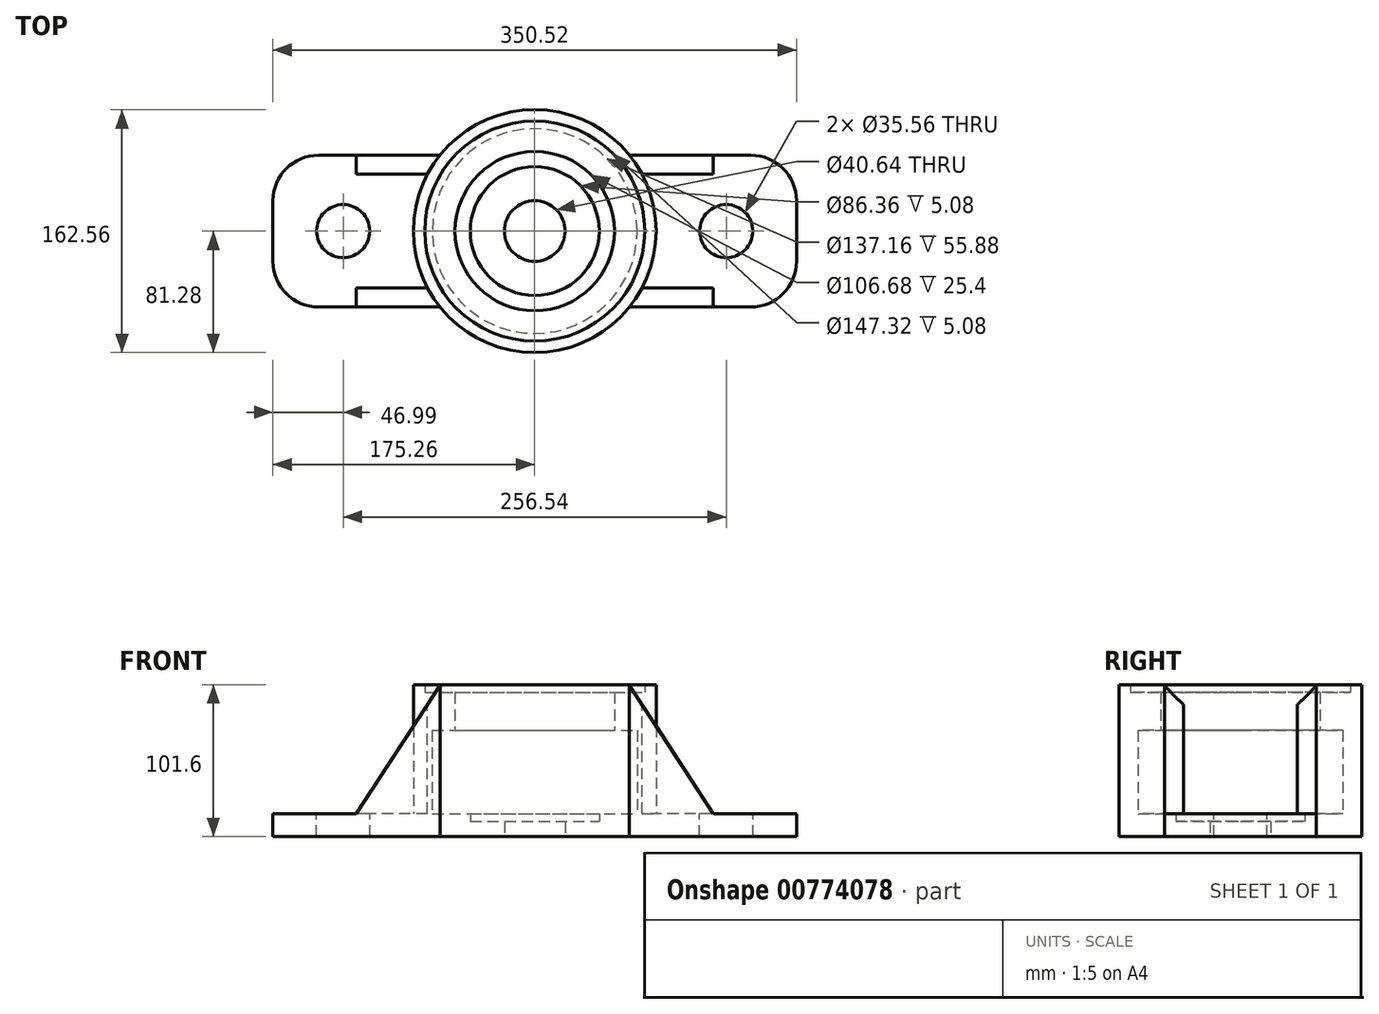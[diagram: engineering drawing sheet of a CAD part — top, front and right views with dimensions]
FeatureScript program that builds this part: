
annotation { "Feature Type Name" : "Feature", "Feature Type Description" : "" }
export const myFeature = defineFeature(function(context is Context, id is Id, definition is map)
    precondition{}
    {
        {
            var Q0;
            Q0=qCreatedBy(makeId("Top.planeOp"),FACE);
            var sketch = newSketch(context, id + "F0", { "sketchPlane" : qUnion([Q0])});
            skLineSegment(sketch, "E0.bottom", {"start": v(175.26, 50.8) * mm, "end": v(-175.26, 50.8) * mm});
            skLineSegment(sketch, "E0.top", {"start": v(175.26, -50.8) * mm, "end": v(-175.26, -50.8) * mm});
            skLineSegment(sketch, "E0.left", {"start": v(175.26, 50.8) * mm, "end": v(175.26, -50.8) * mm});
            skLineSegment(sketch, "E0.right", {"start": v(-175.26, 50.8) * mm, "end": v(-175.26, -50.8) * mm});
            skPoint(sketch, "E0.middle", {"position": v(0, 0) * mm});
            skSolve(sketch);
        }
        {
            var Q0;
            Q0 = qSketchRegion(id + "F0", true);
            extrude(context, id + "F1", {"entities" : qUnion([Q0]), "depth" : 101.6 * mm, "offsetDistance" : 25.4 * mm});
        }
        {
            var Q0;
            Q0=makeQuery(id+"F1.opExtrude","SWEPT_FACE",FACE,{"disambiguationData":[OSD([sQuery(id+"F0.wireOp",EDGE,"E0.top")])]});
            var sketch = newSketch(context, id + "F2", { "sketchPlane" : qUnion([Q0])});
            skLineSegment(sketch, "E1", {"start": v(-175.26, 15.24) * mm, "end": v(-119.38, 15.24) * mm});
            skLineSegment(sketch, "E2", {"start": v(-119.38, 15.24) * mm, "end": v(-63.3, 101.6) * mm});
            skLineSegment(sketch, "E3", {"start": v(63.3, 101.6) * mm, "end": v(119.38, 15.24) * mm});
            skLineSegment(sketch, "E4", {"start": v(119.38, 15.24) * mm, "end": v(175.26, 15.24) * mm});
            skSolve(sketch);
        }
        {
            var Q0;
            {var subQ0=sQuery(id+"F2.wireOp",EDGE,"E1");Q0=makeQuery(id+"F2.imprint","IMPRINT",FACE,{"disambiguationData":[TD([[makeQuery(id+"F2.imprint","IMPRINT",EDGE,{"derivedFrom":subQ0}),1.0]])]});}
            var Q1;
            {var subQ0=sQuery(id+"F2.wireOp",EDGE,"E3");Q1=makeQuery(id+"F2.imprint","IMPRINT",FACE,{"disambiguationData":[TD([[makeQuery(id+"F2.imprint","IMPRINT",EDGE,{"derivedFrom":subQ0}),1.0]])]});}
            extrude(context, id + "F3", {"entities" : qUnion([Q0, Q1]), "operationType" : NewBodyOperationType.REMOVE, "oppositeDirection" : true, "depth" : 135.89 * mm, "offsetDistance" : 25.4 * mm});
        }
        {
            var Q0;
            Q0=makeQuery(id+"F1.opExtrude","CAP_FACE",FACE,{"disambiguationData":[OSD([sQuery(id+"F0.wireOp",EDGE,"E0.bottom"),sQuery(id+"F0.wireOp",EDGE,"E0.top"),sQuery(id+"F0.wireOp",EDGE,"E0.left"),sQuery(id+"F0.wireOp",EDGE,"E0.right")])],"isStart":false});
            var sketch = newSketch(context, id + "F4", { "sketchPlane" : qUnion([Q0])});
            skLineSegment(sketch, "E5.bottom", {"start": v(119.38, 38.1) * mm, "end": v(-119.38, 38.1) * mm});
            skLineSegment(sketch, "E5.top", {"start": v(119.38, -38.1) * mm, "end": v(-119.38, -38.1) * mm});
            skLineSegment(sketch, "E5.left", {"start": v(119.38, 38.1) * mm, "end": v(119.38, -38.1) * mm});
            skLineSegment(sketch, "E5.right", {"start": v(-119.38, 38.1) * mm, "end": v(-119.38, -38.1) * mm});
            skPoint(sketch, "E5.middle", {"position": v(0, 0) * mm});
            skSolve(sketch);
        }
        {
            var Q0;
            {var subQ0=sQuery(id+"F4.wireOp",EDGE,"E5.right");Q0=makeQuery(id+"F4.imprint","IMPRINT",FACE,{"disambiguationData":[TD([[makeQuery(id+"F4.imprint","IMPRINT",EDGE,{"derivedFrom":subQ0}),1.0]])]});}
            var Q1;
            {var subQ0=sQuery(id+"F4.wireOp",EDGE,"E5.bottom");var subQ1=sQuery(id+"F0.wireOp",EDGE,"E0.top");var subQ2=makeQuery(id+"F3.boolean.opBoolean","COPY",EDGE,{"derivedFrom":makeQuery(id+"F3.opExtrude","SWEPT_EDGE",EDGE,{"disambiguationData":[OSD([subQ1,sQuery(id+"F2.wireOp",EDGE,"E3")])]})});var subQ3=makeQuery(id+"F4.imprint","INTERSECT",VERTEX,{"derivedFrom":[subQ2,subQ0]});Q1=makeQuery(id+"F4.imprint","IMPRINT",FACE,{"disambiguationData":[TD([[makeQuery(id+"F4.imprint","IMPRINT",EDGE,{"disambiguationData":[TD([[subQ3,-1.0]])],"derivedFrom":subQ0}),1.0]])]});}
            var Q2;
            {var subQ0=sQuery(id+"F4.wireOp",EDGE,"E5.left");Q2=makeQuery(id+"F4.imprint","IMPRINT",FACE,{"disambiguationData":[TD([[makeQuery(id+"F4.imprint","IMPRINT",EDGE,{"derivedFrom":subQ0}),-1.0]])]});}
            extrude(context, id + "F5", {"entities" : qUnion([Q0, Q1, Q2]), "operationType" : NewBodyOperationType.REMOVE, "oppositeDirection" : true, "depth" : 86.36 * mm, "offsetDistance" : 25.4 * mm});
        }
        {
            var Q0;
            {var subQ0=sQuery(id+"F0.wireOp",EDGE,"E0.top");Q0=makeQuery(id+"F5.boolean.opBoolean","SPLIT",FACE,{"disambiguationData":[TD([makeQuery(id+"F1.opExtrude","SWEPT_FACE",FACE,{"disambiguationData":[OSD([subQ0])]})])],"derivedFrom":makeQuery(id+"F1.opExtrude","CAP_FACE",FACE,{"disambiguationData":[OSD([sQuery(id+"F0.wireOp",EDGE,"E0.bottom"),subQ0,sQuery(id+"F0.wireOp",EDGE,"E0.left"),sQuery(id+"F0.wireOp",EDGE,"E0.right")])],"isStart":false})});}
            var sketch = newSketch(context, id + "F6", { "sketchPlane" : qUnion([Q0])});
            skCircle(sketch, "E6", {"center": v(0, 0) * mm, "radius": 81.28 * mm});
            skSolve(sketch);
        }
        {
            var Q0;
            Q0=makeQuery(id+"F6.imprint","IMPRINT",FACE,{"disambiguationData":[TD([[makeQuery(id+"F6.imprint","IMPRINT",EDGE,{"derivedFrom":sQuery(id+"F6.wireOp",EDGE,"E6")}),1.0]])]});
            var Q1;
            {var subQ0=sQuery(id+"F0.wireOp",EDGE,"E0.top");Q1=makeQuery(id+"F6.imprint","IMPRINT",FACE,{"disambiguationData":[TD([[makeQuery(id+"F6.imprint","IMPRINT",EDGE,{"derivedFrom":makeQuery(id+"F1.opExtrude","CAP_EDGE",EDGE,{"disambiguationData":[OSD([subQ0])],"isStart":false})}),-1.0]])]});}
            extrude(context, id + "F7", {"entities" : qUnion([Q0, Q1]), "operationType" : NewBodyOperationType.REMOVE, "oppositeDirection" : true, "depth" : 214.12 * mm, "offsetDistance" : 25.4 * mm});
        }
        {
            var Q0;
            Q0=qCreatedBy(makeId("Front.planeOp"),FACE);
            var sketch = newSketch(context, id + "F8", { "sketchPlane" : qUnion([Q0])});
            skLineSegment(sketch, "E7", {"start": v(-20.32, 0) * mm, "end": v(-81.28, 0) * mm});
            skLineSegment(sketch, "E8", {"start": v(-81.28, 0) * mm, "end": v(-81.28, 101.6) * mm});
            skLineSegment(sketch, "E9", {"start": v(-81.28, 101.6) * mm, "end": v(-73.66, 101.6) * mm});
            skLineSegment(sketch, "E10", {"start": v(-73.66, 101.6) * mm, "end": v(-73.66, 96.52) * mm});
            skLineSegment(sketch, "E11", {"start": v(-73.66, 96.52) * mm, "end": v(-53.34, 96.52) * mm});
            skLineSegment(sketch, "E12", {"start": v(-53.34, 96.52) * mm, "end": v(-53.34, 71.12) * mm});
            skLineSegment(sketch, "E13", {"start": v(-53.34, 71.12) * mm, "end": v(-68.58, 71.12) * mm});
            skLineSegment(sketch, "E14", {"start": v(-68.58, 71.12) * mm, "end": v(-68.58, 15.24) * mm});
            skLineSegment(sketch, "E15", {"start": v(-68.58, 15.24) * mm, "end": v(-43.18, 15.24) * mm});
            skLineSegment(sketch, "E16", {"start": v(-43.18, 15.24) * mm, "end": v(-43.18, 10.16) * mm});
            skLineSegment(sketch, "E17", {"start": v(-43.18, 10.16) * mm, "end": v(-20.32, 10.16) * mm});
            skLineSegment(sketch, "E18", {"start": v(-20.32, 10.16) * mm, "end": v(-20.32, 0) * mm});
            skSolve(sketch);
        }
        {
            var Q0;
            Q0=qCreatedBy(makeId("Front.planeOp"),FACE);
            var sketch = newSketch(context, id + "F9", { "sketchPlane" : qUnion([Q0])});
            skLineSegment(sketch, "E19", {"start": v(0, 0) * mm, "end": v(0, 100.65) * mm});
            skSolve(sketch);
        }
        {
            var Q0;
            Q0=makeQuery(id+"F8.imprint","IMPRINT",FACE,{"disambiguationData":[TD([[makeQuery(id+"F8.imprint","IMPRINT",EDGE,{"derivedFrom":sQuery(id+"F8.wireOp",EDGE,"E7")}),-1.0]])]});
            var Q1;
            Q1=sQuery(id+"F9.wireOp",EDGE,"E19");
            revolve(context, id + "F10", {"operationType" : NewBodyOperationType.ADD, "surfaceOperationType" : NewSurfaceOperationType.NEW, "entities" : qUnion([Q0]), "axis" : qUnion([Q1]), "revolveType" : RevolveType.FULL});
        }
        {
            var Q0;
            Q0=makeQuery(id+"F1.opExtrude","SWEPT_EDGE",EDGE,{"disambiguationData":[OSD([sQuery(id+"F0.wireOp",EDGE,"E0.top"),sQuery(id+"F0.wireOp",EDGE,"E0.left")])]});
            var Q1;
            Q1=makeQuery(id+"F1.opExtrude","SWEPT_EDGE",EDGE,{"disambiguationData":[OSD([sQuery(id+"F0.wireOp",EDGE,"E0.bottom"),sQuery(id+"F0.wireOp",EDGE,"E0.left")])]});
            var Q2;
            Q2=makeQuery(id+"F1.opExtrude","SWEPT_EDGE",EDGE,{"disambiguationData":[OSD([sQuery(id+"F0.wireOp",EDGE,"E0.top"),sQuery(id+"F0.wireOp",EDGE,"E0.right")])]});
            var Q3;
            Q3=makeQuery(id+"F1.opExtrude","SWEPT_EDGE",EDGE,{"disambiguationData":[OSD([sQuery(id+"F0.wireOp",EDGE,"E0.bottom"),sQuery(id+"F0.wireOp",EDGE,"E0.right")])]});
            fillet(context, id + "F11", {"entities" : qUnion([Q0, Q1, Q2, Q3]), "radius" : 30.48 * mm, "tangentPropagation" : true, "allowEdgeOverflow" : false});
        }
        {
            var Q0;
            {var subQ0=sQuery(id+"F4.wireOp",EDGE,"E5.bottom");var subQ1=sQuery(id+"F4.wireOp",EDGE,"E5.top");Q0=makeQuery(id+"F7.boolean.opBoolean","SPLIT",FACE,{"disambiguationData":[TD([makeQuery(id+"F1.opExtrude","SWEPT_FACE",FACE,{"disambiguationData":[OSD([sQuery(id+"F0.wireOp",EDGE,"E0.right")])]})])],"derivedFrom":makeQuery(id+"F5.boolean.opBoolean","MERGE",FACE,{"derivedFrom":[makeQuery(id+"F3.boolean.opBoolean","COPY",FACE,{"derivedFrom":makeQuery(id+"F3.opExtrude","SWEPT_FACE",FACE,{"disambiguationData":[OSD([sQuery(id+"F2.wireOp",EDGE,"E1")])]})}),makeQuery(id+"F3.boolean.opBoolean","COPY",FACE,{"derivedFrom":makeQuery(id+"F3.opExtrude","SWEPT_FACE",FACE,{"disambiguationData":[OSD([sQuery(id+"F2.wireOp",EDGE,"E4")])]})}),makeQuery(id+"F5.opExtrude","CAP_FACE",FACE,{"disambiguationData":[OSD([subQ0,subQ1,sQuery(id+"F4.wireOp",EDGE,"E5.left"),sQuery(id+"F4.wireOp",EDGE,"E5.right")])],"isStart":false})]})});}
            var sketch = newSketch(context, id + "F12", { "sketchPlane" : qUnion([Q0])});
            skCircle(sketch, "E20", {"center": v(-128.27, 0) * mm, "radius": 17.78 * mm});
            skCircle(sketch, "E21", {"center": v(128.27, 0) * mm, "radius": 17.78 * mm});
            skSolve(sketch);
        }
        {
            var Q0;
            Q0 = qSketchRegion(id + "F12", true);
            extrude(context, id + "F13", {"entities" : qUnion([Q0]), "operationType" : NewBodyOperationType.REMOVE, "oppositeDirection" : true, "depth" : 25.4 * mm, "offsetDistance" : 25.4 * mm});
        }
    });
